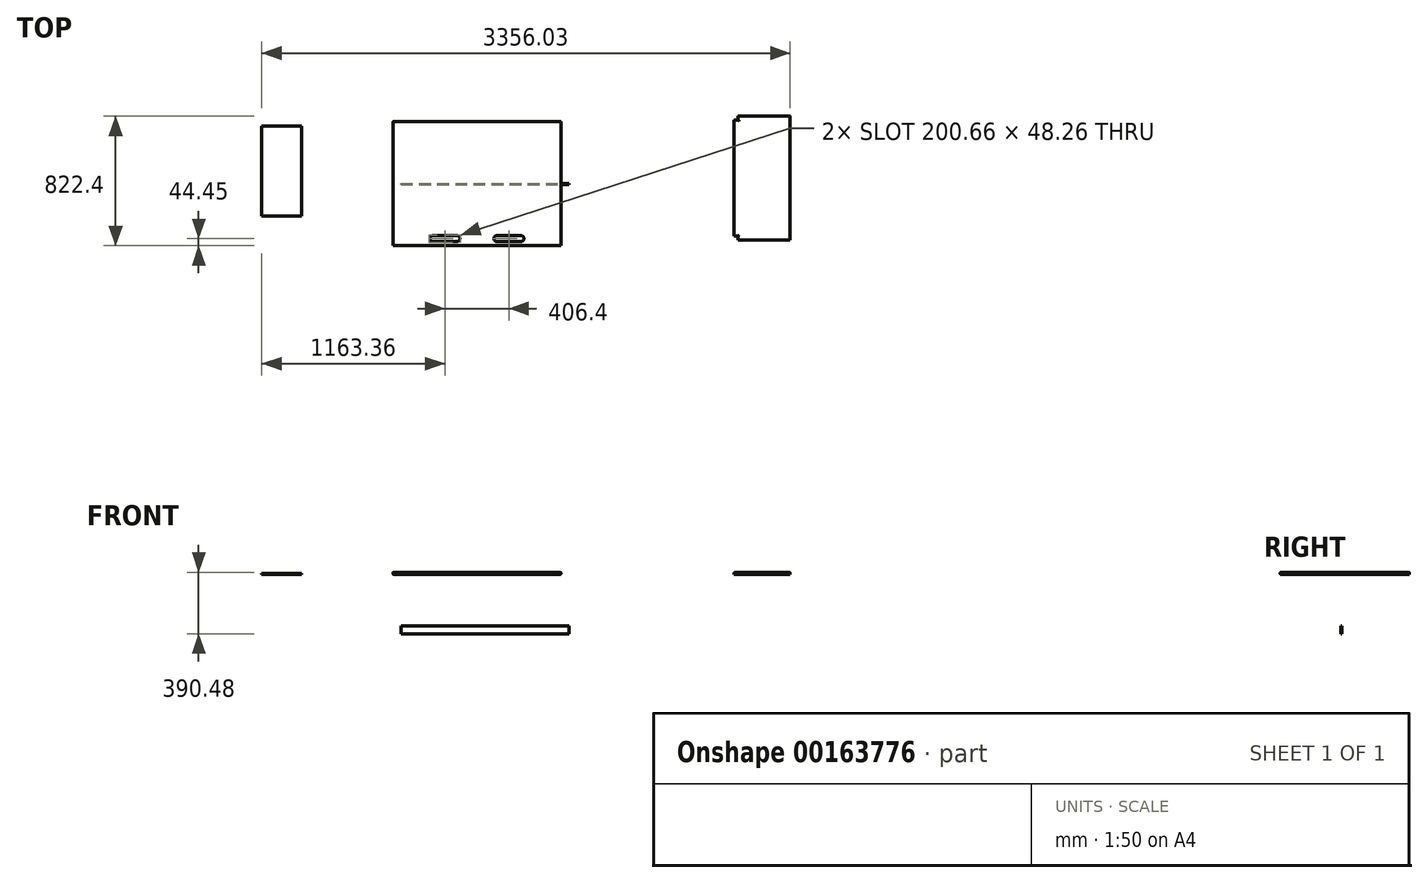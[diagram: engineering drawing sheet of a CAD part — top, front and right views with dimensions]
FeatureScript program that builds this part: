
annotation { "Feature Type Name" : "Feature", "Feature Type Description" : "" }
export const myFeature = defineFeature(function(context is Context, id is Id, definition is map)
    precondition{}
    {
        {
            var Q0;
            Q0=qCreatedBy(makeId("Top.planeOp"),FACE);
            var sketch = newSketch(context, id + "F0", { "sketchPlane" : qUnion([Q0])});
            skLineSegment(sketch, "E0.bottom", {"start": v(533.4, 393.7) * mm, "end": v(-533.4, 393.7) * mm});
            skLineSegment(sketch, "E0.top", {"start": v(533.4, -393.7) * mm, "end": v(-533.4, -393.7) * mm});
            skLineSegment(sketch, "E0.left", {"start": v(533.4, 393.7) * mm, "end": v(533.4, -393.7) * mm});
            skLineSegment(sketch, "E0.right", {"start": v(-533.4, 393.7) * mm, "end": v(-533.4, -393.7) * mm});
            skPoint(sketch, "E0.middle", {"position": v(0, 0) * mm});
            skLineSegment(sketch, "E1.bottom", {"start": v(-279.4, -330.2) * mm, "end": v(-127, -330.2) * mm});
            skLineSegment(sketch, "E1.top", {"start": v(-279.4, -368.3) * mm, "end": v(-127, -368.3) * mm});
            skLineSegment(sketch, "E2", {"start": v(0, 0) * mm, "end": v(0, 500.05) * mm, "construction": true});
            skLineSegment(sketch, "E3.MirrorCS", {"start": v(279.4, -330.2) * mm, "end": v(127, -330.2) * mm});
            skLineSegment(sketch, "E4.MirrorCS", {"start": v(279.4, -368.3) * mm, "end": v(127, -368.3) * mm});
            skArc(sketch, "E5", {"start": v(-279.4, -330.2) * mm, "mid": v(-298.45, -349.25) * mm, "end": v(-279.4, -368.3) * mm});
            skArc(sketch, "E6", {"start": v(-127, -368.3) * mm, "mid": v(-107.95, -349.25) * mm, "end": v(-127, -330.2) * mm});
            skArc(sketch, "E7", {"start": v(127, -330.2) * mm, "mid": v(107.95, -349.25) * mm, "end": v(127, -368.3) * mm});
            skArc(sketch, "E8", {"start": v(279.4, -368.3) * mm, "mid": v(298.45, -349.25) * mm, "end": v(279.4, -330.2) * mm});
            skPoint(sketch, "E9.orphan", {"position": v(127, -368.3) * mm});
            skPoint(sketch, "E10.MirrorCS.start.orphan", {"position": v(127, -330.2) * mm});
            skPoint(sketch, "E11.orphan", {"position": v(279.4, -368.3) * mm});
            skPoint(sketch, "E12.MirrorCS.start.orphan", {"position": v(279.4, -330.2) * mm});
            skSolve(sketch);
        }
        {
            var Q0;
            Q0=qSketchRegion(id+"F0",true);
            extrude(context, id + "F1", {"entities" : qUnion([Q0]), "depth" : 12.7 * mm, "offsetDistance" : 25.4 * mm});
        }
        {
            var Q0;
            Q0=makeQuery(id+"F1.opExtrude","CAP_FACE",FACE,{"disambiguationData":[OSD([sQuery(id+"F0.wireOp",EDGE,"E0.bottom"),sQuery(id+"F0.wireOp",EDGE,"E0.top"),sQuery(id+"F0.wireOp",EDGE,"E0.left"),sQuery(id+"F0.wireOp",EDGE,"E0.right")])],"isStart":false});
            fillet(context, id + "F2", {"entities" : qUnion([Q0]), "radius" : 5.08 * mm, "tangentPropagation" : true, "allowEdgeOverflow" : false});
        }
        {
            var Q0;
            Q0=makeQuery(id+"F1.opExtrude","CAP_FACE",FACE,{"disambiguationData":[OSD([sQuery(id+"F0.wireOp",EDGE,"E0.bottom"),sQuery(id+"F0.wireOp",EDGE,"E0.top"),sQuery(id+"F0.wireOp",EDGE,"E0.left"),sQuery(id+"F0.wireOp",EDGE,"E0.right"),sQuery(id+"F0.wireOp",EDGE,"E1.bottom"),sQuery(id+"F0.wireOp",EDGE,"E1.top"),sQuery(id+"F0.wireOp",EDGE,"E3.MirrorCS"),sQuery(id+"F0.wireOp",EDGE,"E4.MirrorCS"),sQuery(id+"F0.wireOp",EDGE,"E5"),sQuery(id+"F0.wireOp",EDGE,"E6"),sQuery(id+"F0.wireOp",EDGE,"E7"),sQuery(id+"F0.wireOp",EDGE,"E8")])],"isStart":true});
            fillet(context, id + "F3", {"entities" : qUnion([Q0]), "radius" : 5.08 * mm, "tangentPropagation" : true, "allowEdgeOverflow" : false});
        }
        {
            var Q0;
            Q0=qCreatedBy(makeId("Front.planeOp"),FACE);
            var sketch = newSketch(context, id + "F4", { "sketchPlane" : qUnion([Q0])});
            skLineSegment(sketch, "E13.bottom", {"start": v(-482.11, -326.98) * mm, "end": v(584.69, -326.98) * mm});
            skLineSegment(sketch, "E13.top", {"start": v(-482.11, -377.78) * mm, "end": v(584.69, -377.78) * mm});
            skLineSegment(sketch, "E13.left", {"start": v(-482.11, -326.98) * mm, "end": v(-482.11, -377.78) * mm});
            skLineSegment(sketch, "E13.right", {"start": v(584.69, -326.98) * mm, "end": v(584.69, -377.78) * mm});
            skSolve(sketch);
        }
        {
            var Q0;
            Q0 = qSketchRegion(id + "F4", true);
            extrude(context, id + "F5", {"entities" : qUnion([Q0]), "depth" : 6.35 * mm, "offsetDistance" : 25.4 * mm});
        }
        {
            var Q0;
            Q0=qCreatedBy(makeId("Top.planeOp"),FACE);
            var sketch = newSketch(context, id + "F6", { "sketchPlane" : qUnion([Q0])});
            skLineSegment(sketch, "E14.bottom", {"start": v(1659.27, 428.7) * mm, "end": v(1989.47, 428.7) * mm});
            skLineSegment(sketch, "E14.top", {"start": v(1659.27, -358.7) * mm, "end": v(1989.47, -358.7) * mm});
            skLineSegment(sketch, "E14.left", {"start": v(1633.87, 403.3) * mm, "end": v(1633.87, -333.3) * mm});
            skLineSegment(sketch, "E14.right", {"start": v(1989.47, 428.7) * mm, "end": v(1989.47, -358.7) * mm});
            skLineSegment(sketch, "E15.top", {"start": v(1633.87, -333.3) * mm, "end": v(1659.27, -333.3) * mm});
            skLineSegment(sketch, "E15.right", {"start": v(1659.27, -358.7) * mm, "end": v(1659.27, -333.3) * mm});
            skLineSegment(sketch, "E16.top", {"start": v(1633.87, 403.3) * mm, "end": v(1659.27, 403.3) * mm});
            skLineSegment(sketch, "E16.right", {"start": v(1659.27, 428.7) * mm, "end": v(1659.27, 403.3) * mm});
            skSolve(sketch);
        }
        {
            var Q0;
            Q0 = qSketchRegion(id + "F6", true);
            extrude(context, id + "F7", {"entities" : qUnion([Q0]), "depth" : 12.7 * mm, "offsetDistance" : 25.4 * mm});
        }
        {
            var Q0;
            Q0=makeQuery(id+"F7.opExtrude","CAP_FACE",FACE,{"disambiguationData":[OSD([sQuery(id+"F6.wireOp",EDGE,"E14.bottom"),sQuery(id+"F6.wireOp",EDGE,"E14.top"),sQuery(id+"F6.wireOp",EDGE,"E14.left"),sQuery(id+"F6.wireOp",EDGE,"E14.right"),sQuery(id+"F6.wireOp",EDGE,"E15.top"),sQuery(id+"F6.wireOp",EDGE,"E15.right"),sQuery(id+"F6.wireOp",EDGE,"E16.top"),sQuery(id+"F6.wireOp",EDGE,"E16.right")])],"isStart":false});
            fillet(context, id + "F8", {"entities" : qUnion([Q0]), "radius" : 5.08 * mm, "tangentPropagation" : true, "allowEdgeOverflow" : false});
        }
        {
            var Q0;
            Q0=qCreatedBy(makeId("Top.planeOp"),FACE);
            var sketch = newSketch(context, id + "F9", { "sketchPlane" : qUnion([Q0])});
            skLineSegment(sketch, "E17.bottom", {"start": v(-1366.56, 364.85) * mm, "end": v(-1112.56, 364.85) * mm});
            skLineSegment(sketch, "E17.top", {"start": v(-1366.56, -206.65) * mm, "end": v(-1112.56, -206.65) * mm});
            skLineSegment(sketch, "E17.left", {"start": v(-1366.56, 364.85) * mm, "end": v(-1366.56, -206.65) * mm});
            skLineSegment(sketch, "E17.right", {"start": v(-1112.56, 364.85) * mm, "end": v(-1112.56, -206.65) * mm});
            skSolve(sketch);
        }
        {
            var Q0;
            Q0 = qSketchRegion(id + "F9", true);
            extrude(context, id + "F10", {"entities" : qUnion([Q0]), "depth" : 6.35 * mm, "offsetDistance" : 25.4 * mm});
        }
    });
